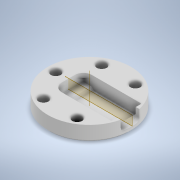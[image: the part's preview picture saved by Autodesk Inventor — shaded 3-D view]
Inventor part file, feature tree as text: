
AUTODESK INVENTOR PART (.ipt)
format: ipt  version: 2021 (Build 250183000, 183)  size: 899,584 bytes
history: native  units: in
note: dims shown in document units (in); Inventor stores cm internally (conversion verified against a paired STEP export)
features: extrude x6, sketch x6, fillet x4, chamfer x3, other x1, plane x1, pattern_circular x1, mirror x1
ambient origin geometry x8: Origin, YZ Plane, XZ Plane, XY Plane, X Axis, Y Axis, Z Axis, Center Point
bodies: Solid1 (feature_tree)
feature tree (23):
  extrude  "Extrusion1"  Depth=0.378in TaperAngle=0.0deg
  chamfer  "Chamfer2"  Distance=0.252in
  extrude  "Extrusion2"  Depth=0.1417in
  extrude  "Extrusion3"  TaperAngle=0.0deg  [1 undecoded]
  other  "Work Axis1"
  plane  "Work Plane1"
  extrude  "Extrusion5"  Depth=0.2224in
  extrude  "Extrusion4"  Depth=0.2047in TaperAngle=0.0deg
  fillet  "Fillet4"  Radius=0.8268in
  pattern_circular  "Circular Pattern2"  [2 undecoded]
  fillet  "Fillet7"  Radius=0.1969in
  extrude  "Initals"  Depth=0.063in TaperAngle=0.0deg
  fillet  "Fillet9"  Radius=0.1417in
  fillet  "Fillet10"  [1 undecoded]
  mirror  "Mirror6"
  chamfer  "Chamfer4"  Angle=45.0deg  [1 undecoded]
  chamfer  "Chamfer5"  Distance=0.0394in
  sketch  "Sketch1"  dims[d0=2.0472in d3=0.378in d4=0.0in]
  sketch  "Sketch2"  dims[d5=1.4315in]
  sketch  "Sketch3"  dims[d6=0.7394in]
  sketch  "Sketch4"  dims[d7=0.3697in]
  sketch  "Sketch7"  dims[d8=0.5197in d9=0.252in d10=0.0in]
  sketch  "Sketch12"  dims[d11=0.0in d14=0.1417in d15=0.0in d16=0.0in d17=0.2224in d18=0.2047in d19=0.0in d23=0.8268in d24=0.3697in d31=0.1969in d32=0.063in d33=0.0in d44=0.1417in d47=0.0in d48=0.0in d49=0.0in d51=0.0in d54=0.0551in d55=0.0in d56=45.0deg d58=0.0394in d59=0.1181in d60=1.9685in d61=240.0deg d72=0.0315in d80=1.9685in d81=0.9843in d82=0.9728in d83=0.4864in d84=0.0394in d85=0.0in d90=0.0787in d98=0.1024in d99=0.0in d100=0.0in d101=0.2362in d102=0.0315in d103=0.0315in d104=0.2953in d105=0.1575in d106=0.1969in d107=0.063in d108=0.0787in d109=45.0deg d110=0.063in d111=0.0787in d112=45.0deg d91=0.0197in d92=0.0344in d93=0.0197in d94=0.0344in d120=0.0197in d121=0.0344in d122=0.0197in d123=0.0344in]
note: 5 required parameter values undecoded (feature->parameter linkage not recoverable at this tier; creation-order binding heuristic only, values carry confidence <= 0.55)
